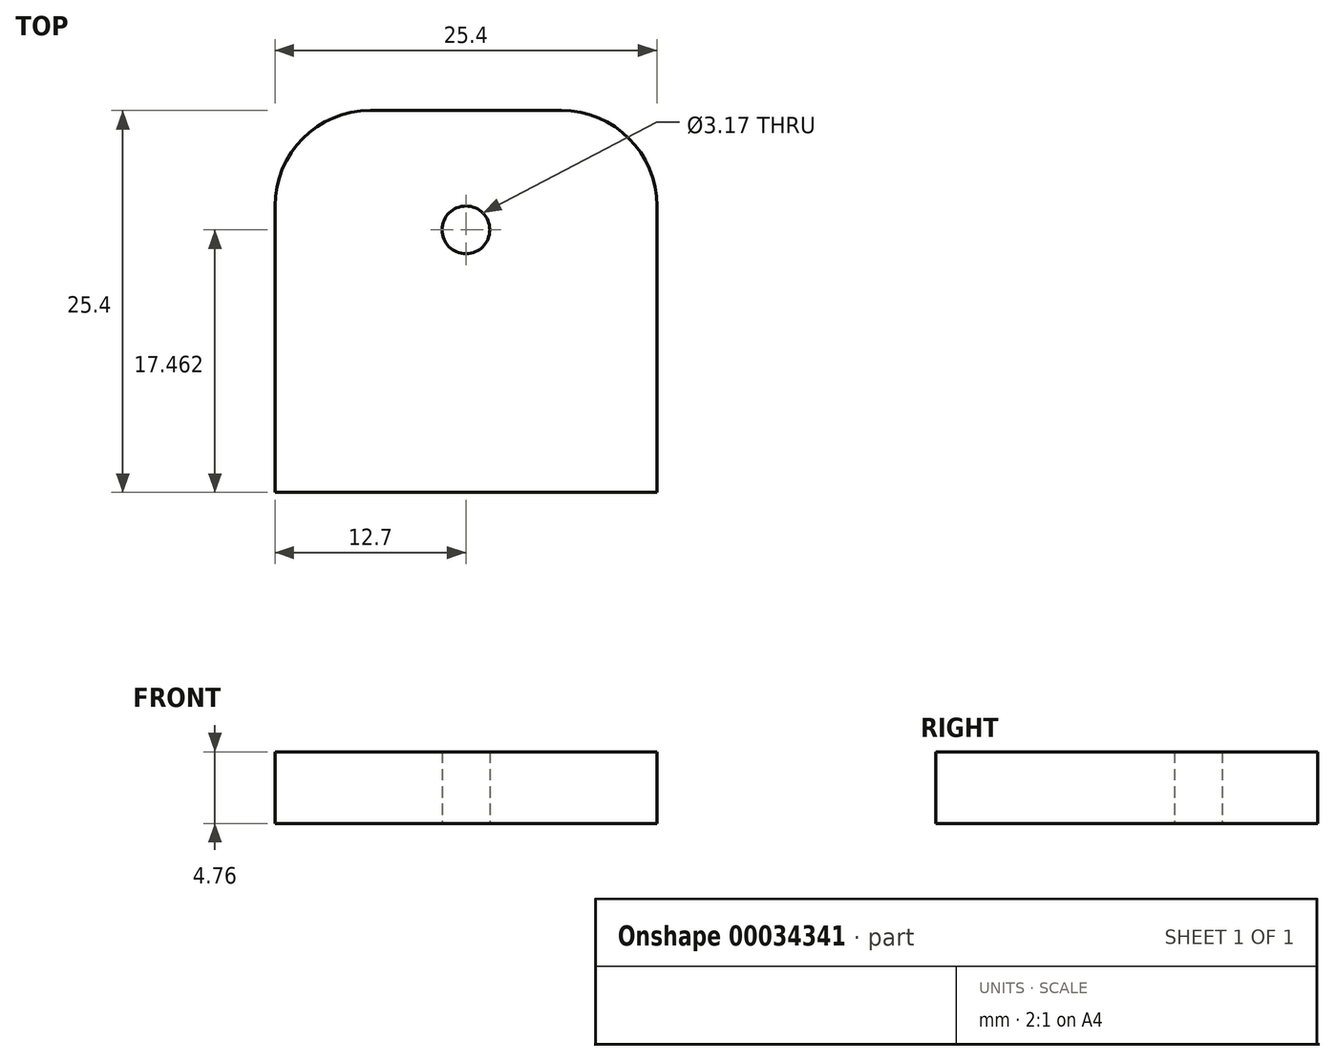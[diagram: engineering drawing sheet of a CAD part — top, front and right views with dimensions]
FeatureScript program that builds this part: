
annotation { "Feature Type Name" : "Feature", "Feature Type Description" : "" }
export const myFeature = defineFeature(function(context is Context, id is Id, definition is map)
    precondition{}
    {
        {
            var Q0;
            Q0=qCreatedBy(makeId("Top.planeOp"),FACE);
            var sketch = newSketch(context, id + "F0", { "sketchPlane" : qUnion([Q0])});
            skCircle(sketch, "E0", {"center": v(0, 17.46) * mm, "radius": 1.59 * mm});
            skLineSegment(sketch, "E1", {"start": v(-12.7, 0) * mm, "end": v(12.7, 0) * mm});
            skLineSegment(sketch, "E2", {"start": v(-12.7, 0) * mm, "end": v(-12.7, 25.4) * mm});
            skLineSegment(sketch, "E3", {"start": v(-12.7, 25.4) * mm, "end": v(12.7, 25.4) * mm});
            skLineSegment(sketch, "E4", {"start": v(12.7, 25.4) * mm, "end": v(12.7, 0) * mm});
            skSolve(sketch);
        }
        {
            var Q0;
            Q0 = qSketchRegion(id + "F0", true);
            extrude(context, id + "F1", {"entities" : qUnion([Q0]), "depth" : 4.76 * mm});
        }
        {
            var Q0;
            Q0=makeQuery(id+"F1.opExtrude","SWEPT_EDGE",EDGE,{"disambiguationData":[OSD([sQuery(id+"F0.wireOp",EDGE,"E2"),sQuery(id+"F0.wireOp",EDGE,"E3")])]});
            var Q1;
            Q1=makeQuery(id+"F1.opExtrude","SWEPT_EDGE",EDGE,{"disambiguationData":[OSD([sQuery(id+"F0.wireOp",EDGE,"E3"),sQuery(id+"F0.wireOp",EDGE,"E4")])]});
            fillet(context, id + "F2", {"entities" : qUnion([Q0, Q1]), "radius" : 6.35 * mm, "tangentPropagation" : true, "allowEdgeOverflow" : false});
        }
    });
